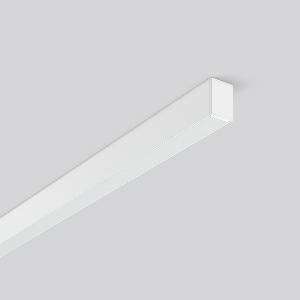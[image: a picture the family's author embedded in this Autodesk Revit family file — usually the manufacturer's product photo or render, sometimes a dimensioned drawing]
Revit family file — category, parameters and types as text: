
# Revit family: less_is_more_27_312200_002_76_c8f8
name_source: partatom
category: Lighting Fixtures
units: mm (PartAtom-declared; Revit-internal decimal feet)

## family parameters
Cut with Voids When Loaded = No
Host = Face
Light Source = No
Part Type = Normal
Room Calculation Point = No
Round Connector Dimension = Use Diameter
Shared = No

## types (1)
- LESS IS MORE 27 (1 x LED Modul 830, 2900 lm, 3000)
    Apparent Load = 43 VA
    CIE Flux Codes = 48 79 96 100 100
    Color Rendering = 80
    Color Temperature = 3000
    Default Elevation = 1800 mm
    Description = Series: LESS IS MORE 27
Ceiling and wall luminaire with slim design. Housing: extruded aluminium profile, powder-coated. End cap aluminium powder-coated. Diffuser made of non-yellowing plastic (PMMA), opal. Suitable for Ceiling mounting, Wall (surface). External driver with connecting cable. 
Colour: traffic white, matt (RAL 9016)
Length: 1512 mm
Width: 28 mm
Height: 38 mm
Lamp: LED
Socket: without socket
Colour temperature: 3000K
Colour rendering index (CRI): 82
System power: 43 W
Rated luminous flux: 2900 lm
Luminous efficiency: 67 lm/W
Control gear: Voltage converter, DALI dim.
Protection class: II
Type of protection: IP 20
    Height = 38 mm
    Lamp = 1 x LED Modul 830
    Lamp Light Flux = 2900 lm
    Lamp count = 1
    Length = 1512 mm
    Lifetime = 50000 h
    Luminous efficacy = 67 lm/W
    Manufacturer = RZB
    ModVariant = No
    Model = 312200.002.76
    Mounting Place = Ceiling, Wall
    Mounting Type = Surface mounted
    Number of Poles = 1
    OnlyDefault = Yes
    Power Factor = 1
    Product Name = LESS IS MORE 27
    Product group = Surface mounted LED linear luminaires
    ProductGroupID = 307
    Protection Class = Protection class II
    Protection Degree = IP 20
    RLX_Detail_Level = 1
    RLX_Emergency_Light_Flux = 0 lm
    RLX_Emergency_Type = 0
    RLX_Emergency_Type_DB = No
    RlxData = <blob elided: 22797 chars, md5=692cfd46>
    Socket = socket
    Standby Power = 0 W
    System Light Flux = 2900 lm
    System Power = 43 W
    Type Comments = Product without accessories
    Type Image = 312196.002.jpg
    URL = http://relux.com
    VarID = ---
    Voltage = 230 V
    Voltage Range = 220-240 V
    Weight = 0.00 kg
    Width = 28 mm

## geometry (parser evidence)
native form markers: Blend x4, Sweep x11
no freeform markers — native parametric forms only
